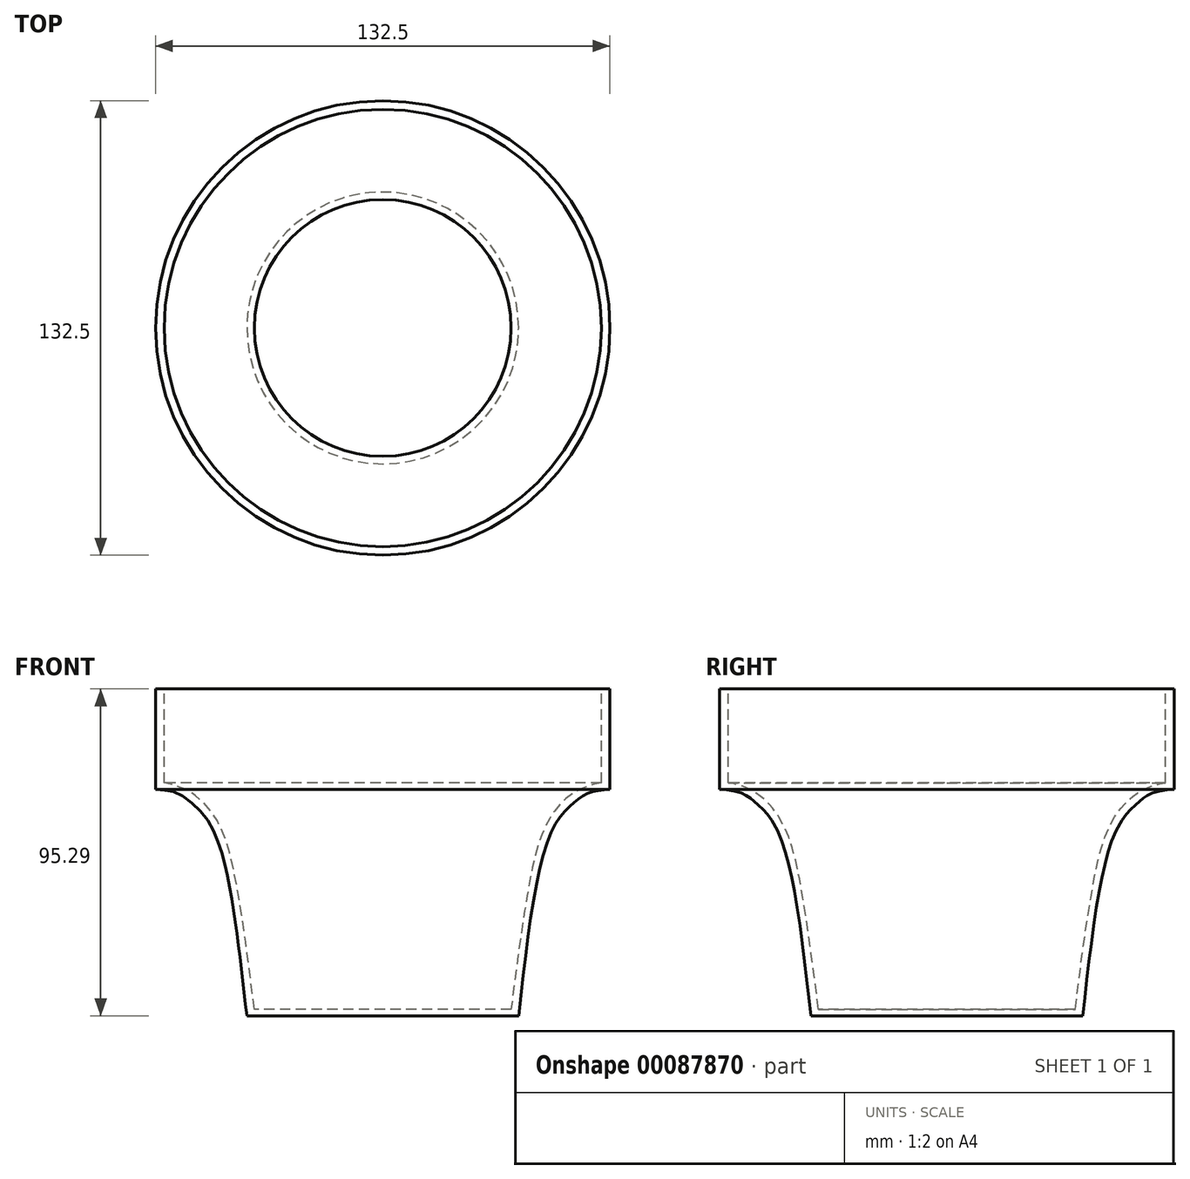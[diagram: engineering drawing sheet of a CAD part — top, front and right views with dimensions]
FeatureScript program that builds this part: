
annotation { "Feature Type Name" : "Feature", "Feature Type Description" : "" }
export const myFeature = defineFeature(function(context is Context, id is Id, definition is map)
    precondition{}
    {
        {
            var Q0;
            Q0=qCreatedBy(makeId("Front.planeOp"),FACE);
            var sketch = newSketch(context, id + "F0", { "sketchPlane" : qUnion([Q0])});
            skLineSegment(sketch, "E0", {"start": v(0, -75.78) * mm, "end": v(-39.63, -75.78) * mm});
            skFitSpline(sketch, "E1", {"points": [v(-39.63, -75.78) * mm, v(-49, -22.54) * mm, v(-55.66, -13.76) * mm, v(-60.2, -10.74) * mm, v(-66.25, -9.83) * mm], "startDerivative": vector(-15.33, 135.9) * mm, "endDerivative": vector(-40.14, 2.35) * mm});
            skLineSegment(sketch, "E2", {"start": v(-66.25, -9.83) * mm, "end": v(-66.25, 19.51) * mm});
            skLineSegment(sketch, "E3", {"start": v(-66.25, 19.51) * mm, "end": v(-63.76, 19.51) * mm});
            skLineSegment(sketch, "E4", {"start": v(-63.76, 19.51) * mm, "end": v(-63.76, -7.82) * mm});
            skFitSpline(sketch, "E5", {"points": [v(-63.76, -7.82) * mm, v(-57.97, -9.52) * mm, v(-52.11, -13.76) * mm, v(-47.6, -20.2) * mm, v(-43.95, -31.18) * mm, v(-40, -54.26) * mm, v(-37.44, -73.91) * mm], "startDerivative": vector(48.95, -10.41) * mm, "endDerivative": vector(10.87, -87.02) * mm});
            skLineSegment(sketch, "E6", {"start": v(-37.44, -73.91) * mm, "end": v(0, -73.91) * mm});
            skLineSegment(sketch, "E7", {"start": v(0, -73.91) * mm, "end": v(0, -75.78) * mm});
            skSolve(sketch);
        }
        {
            var Q0;
            Q0=makeQuery(id+"F0.imprint","IMPRINT",FACE,{"disambiguationData":[TD([[makeQuery(id+"F0.imprint","IMPRINT",EDGE,{"derivedFrom":sQuery(id+"F0.wireOp",EDGE,"E0")}),-1.0]])]});
            var Q1;
            Q1=sQuery(id+"F0.wireOp",EDGE,"E7");
            revolve(context, id + "F1", {"entities" : qUnion([Q0]), "axis" : qUnion([Q1]), "revolveType" : RevolveType.FULL});
        }
    });
